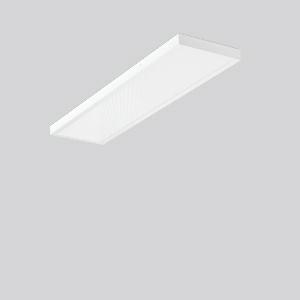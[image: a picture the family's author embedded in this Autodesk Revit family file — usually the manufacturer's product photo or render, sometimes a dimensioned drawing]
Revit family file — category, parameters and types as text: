
# Revit family: sidelite_eco_312379_002_1_76_5f20
name_source: partatom
category: Lighting Fixtures
units: mm (PartAtom-declared; Revit-internal decimal feet)

## family parameters
Cut with Voids When Loaded = No
Host = Face
Light Source = No
Part Type = Normal
Room Calculation Point = No
Round Connector Dimension = Use Diameter
Shared = No

## types (1)
- MultiLumen 1 (1 x LED Modul 840, 3500 lm, 4000)
    Apparent Load = 29 VA
    CIE Flux Codes = 63 88 97 100 100
    Color Rendering = 80
    Color Temperature = 4000
    Default Elevation = 1800 mm
    Description = Series: SIDELITE ECO
Highly economical surface mounted luminaire with progressive LED technology. Luminaire frame: aluminium, powder-coated. Mounting frame: sheet steel, powder-coated. Diffuser plastic microprismatic. Lightguide and diffuser made of non-yellowing plastic (PMMA). Lateral light emission (RZB SIDELITE technology) for homogeneous light distribution. Driver integrated. MultiLumen: 4 steps adjustable luminous flux. Factory setting is the lowest offered step. Perfect for office areas (RUG < 19) and environments with computer screens in accordance with EN 12464-1. Qualified for use in the food and drink industry. 
Colour: white
Length: 1202 mm
Width: 302 mm
Height: 47 mm
Lamp: LED
Socket: without socket
Colour temperature: 4000K
Colour rendering index (CRI): 80
System power: 29 W
Rated luminous flux: 3500 lm
Luminous efficiency: 121 lm/W
System power 2: 33 W
Rated luminous flux 2: 3850 lm
Luminous efficiency 2: 117 lm/W
System power 3: 35 W
Rated luminous flux 3: 4050 lm
Luminous efficiency 3: 116 lm/W
System power 4: 38 W
Rated luminous flux 4: 4400 lm
Luminous efficiency 4: 116 lm/W
Control gear: Converter, dimmable, DALI
Protection class: II
Type of protection: IP 40
    Height = 47 mm
    Lamp = 1 x LED Modul 840
    Lamp Light Flux = 3500 lm
    Lamp count = 1
    Length = 1202 mm
    Lifetime = 50000 h
    Luminous efficacy = 121 lm/W
    Manufacturer = RZB
    ModVariant = No
    Model = 312379.002.1.76
    Mounting Place = Ceiling
    Mounting Type = Surface mounted
    Number of Poles = 1
    OnlyDefault = Yes
    Power Factor = 1
    Product Name = SIDELITE ECO
    Product group = Surface mounted modular luminaires
    ProductGroupID = 306
    Protection Class = Protection class II
    Protection Degree = IP 40
    RLX_Detail_Level = 1
    RLX_Emergency_Light_Flux = 0 lm
    RLX_Emergency_Type = 0
    RLX_Emergency_Type_DB = No
    RlxData = <blob elided: 23573 chars, md5=3e53f9b8>
    Socket = socket
    Standby Power = 0 W
    System Light Flux = 3500 lm
    System Power = 29 W
    Type Comments = MultiLumen 1
    Type Image = 312379.002.jpg
    URL = http://relux.com
    VarID = multilumen_1
    Voltage = 230 V
    Voltage Range = 220-240 V
    Weight = 0.00 kg
    Width = 302 mm

## geometry (parser evidence)
native form markers: Blend x4, Sweep x11
no freeform markers — native parametric forms only
